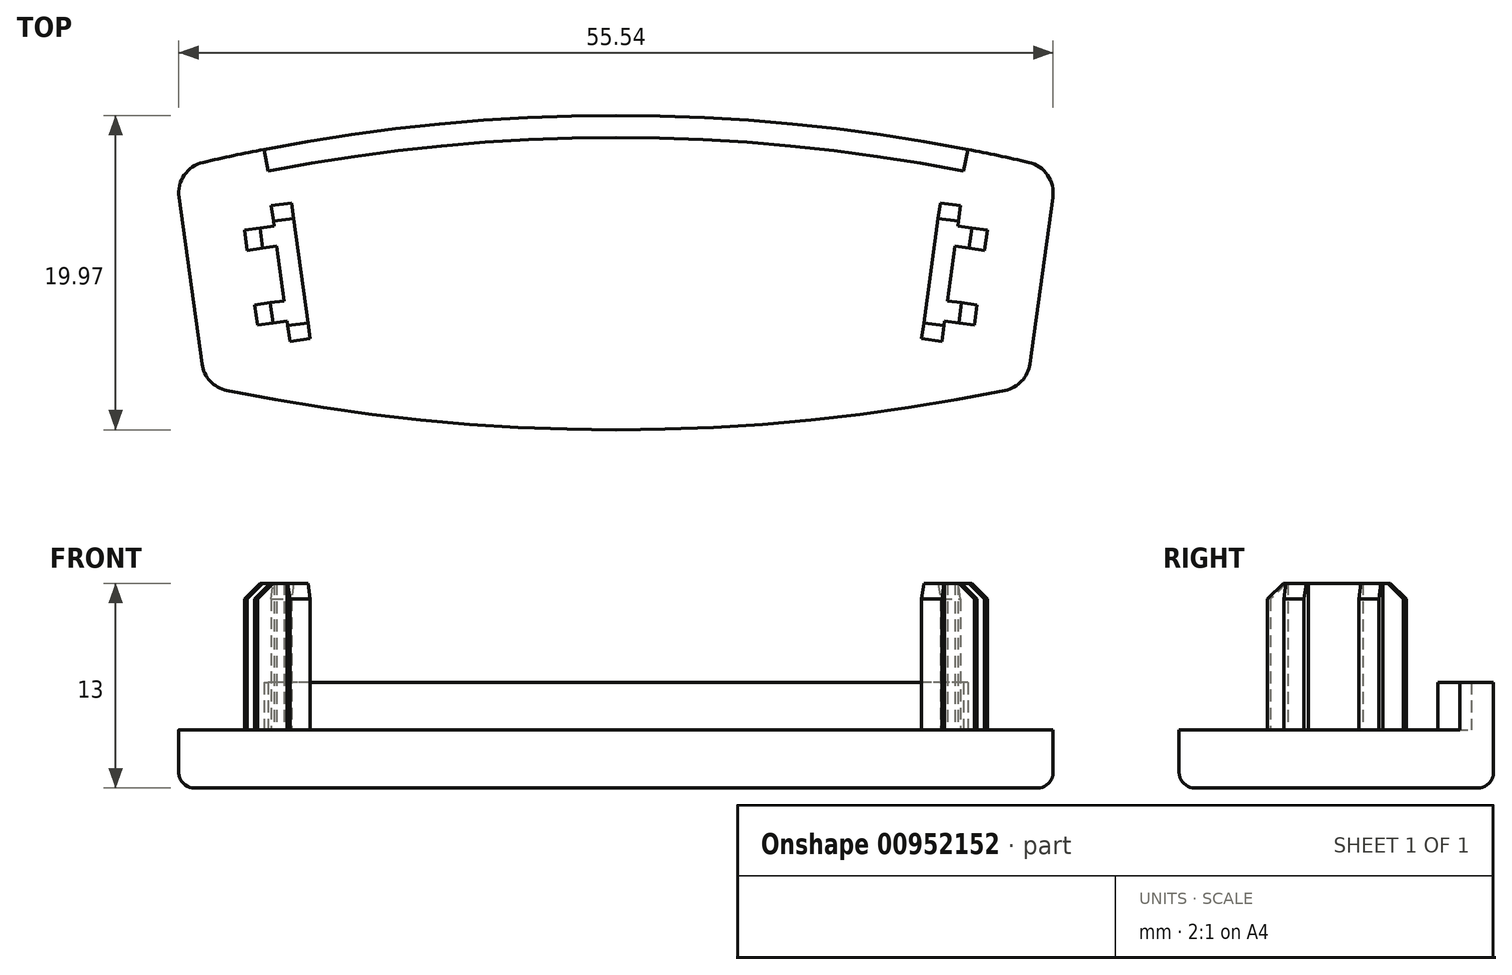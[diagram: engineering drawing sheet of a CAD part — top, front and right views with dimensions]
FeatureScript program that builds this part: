
annotation { "Feature Type Name" : "Feature", "Feature Type Description" : "" }
export const myFeature = defineFeature(function(context is Context, id is Id, definition is map)
    precondition{}
    {
        {
            var Q0;
            Q0=qCreatedBy(makeId("Top.planeOp"),FACE);
            var sketch = newSketch(context, id + "F0", { "sketchPlane" : qUnion([Q0])});
            skLineSegment(sketch, "E0", {"start": v(0, 0) * mm, "end": v(0, -117) * mm, "construction": true});
            skArc(sketch, "E1", {"start": v(28, -3.4) * mm, "mid": v(14.1, -0.85) * mm, "end": v(0, 0) * mm});
            skLineSegment(sketch, "E2", {"start": v(28, -3.4) * mm, "end": v(26.1, -17.17) * mm});
            skArc(sketch, "E3", {"start": v(0, -19.97) * mm, "mid": v(13.12, -19.27) * mm, "end": v(26.1, -17.17) * mm});
            skArc(sketch, "E4.MirrorCS", {"start": v(-28, -3.4) * mm, "mid": v(-14.1, -0.85) * mm, "end": v(0, 0) * mm});
            skLineSegment(sketch, "E5.MirrorCS", {"start": v(-28, -3.4) * mm, "end": v(-26.1, -17.17) * mm});
            skArc(sketch, "E6.MirrorCS", {"start": v(0, -19.97) * mm, "mid": v(-13.12, -19.27) * mm, "end": v(-26.1, -17.17) * mm});
            skSolve(sketch);
        }
        {
            var Q0;
            Q0 = qSketchRegion(id + "F0", true);
            extrude(context, id + "F1", {"entities" : qUnion([Q0]), "oppositeDirection" : true, "depth" : 3.7 * mm, "offsetDistance" : 25 * mm});
        }
        {
            var Q0;
            Q0=makeQuery(id+"F1.opExtrude","CAP_FACE",FACE,{"disambiguationData":[OSD([sQuery(id+"F0.wireOp",EDGE,"E1"),sQuery(id+"F0.wireOp",EDGE,"E2"),sQuery(id+"F0.wireOp",EDGE,"E3"),sQuery(id+"F0.wireOp",EDGE,"E4.MirrorCS"),sQuery(id+"F0.wireOp",EDGE,"E5.MirrorCS"),sQuery(id+"F0.wireOp",EDGE,"E6.MirrorCS")])],"isStart":true});
            var sketch = newSketch(context, id + "F2", { "sketchPlane" : qUnion([Q0])});
            skArc(sketch, "E7", {"start": v(22.35, -2.15) * mm, "mid": v(0, 0) * mm, "end": v(-22.35, -2.15) * mm});
            skPoint(sketch, "E8.end.orphan", {"position": v(-28, -3.4) * mm});
            skPoint(sketch, "E9.0.start.orphan", {"position": v(28, -3.4) * mm});
            skLineSegment(sketch, "E10", {"start": v(0, 0) * mm, "end": v(0, -19.97) * mm, "construction": true});
            skArc(sketch, "E11.0", {"start": v(22.08, -3.53) * mm, "mid": v(0, -1.4) * mm, "end": v(-22.08, -3.53) * mm});
            skLineSegment(sketch, "E12", {"start": v(-22.35, -2.15) * mm, "end": v(-22.08, -3.53) * mm});
            skLineSegment(sketch, "E13", {"start": v(22.35, -2.15) * mm, "end": v(22.08, -3.53) * mm});
            skPoint(sketch, "E14", {"position": v(0, -7.1) * mm});
            skLineSegment(sketch, "E15", {"start": v(0, -7.1) * mm, "end": v(21.3, -10.04) * mm, "construction": true});
            skLineSegment(sketch, "E16", {"start": v(21.9, -5.73) * mm, "end": v(20.7, -14.35) * mm});
            skLineSegment(sketch, "E17.0", {"start": v(20.6, -5.55) * mm, "end": v(19.42, -14.17) * mm});
            skLineSegment(sketch, "E18", {"start": v(21.9, -5.73) * mm, "end": v(20.6, -5.55) * mm});
            skLineSegment(sketch, "E19", {"start": v(20.7, -14.35) * mm, "end": v(19.42, -14.17) * mm});
            skLineSegment(sketch, "E20", {"start": v(21.72, -7.02) * mm, "end": v(23.6, -7.28) * mm});
            skLineSegment(sketch, "E21", {"start": v(23.6, -7.28) * mm, "end": v(23.42, -8.56) * mm});
            skLineSegment(sketch, "E22", {"start": v(23.42, -8.56) * mm, "end": v(21.54, -8.3) * mm});
            skLineSegment(sketch, "E23.MirrorCS", {"start": v(20.88, -13.06) * mm, "end": v(22.76, -13.32) * mm});
            skLineSegment(sketch, "E24.MirrorCS", {"start": v(22.76, -13.32) * mm, "end": v(22.94, -12.03) * mm});
            skLineSegment(sketch, "E25.MirrorCS", {"start": v(22.94, -12.03) * mm, "end": v(21.06, -11.77) * mm});
            skLineSegment(sketch, "E26.MirrorCS", {"start": v(-20.6, -5.55) * mm, "end": v(-19.42, -14.17) * mm});
            skLineSegment(sketch, "E27.MirrorCS", {"start": v(-21.9, -5.73) * mm, "end": v(-20.6, -5.55) * mm});
            skLineSegment(sketch, "E28.MirrorCS", {"start": v(-21.9, -5.73) * mm, "end": v(-20.7, -14.35) * mm});
            skLineSegment(sketch, "E29.MirrorCS", {"start": v(-21.72, -7.02) * mm, "end": v(-23.6, -7.28) * mm});
            skLineSegment(sketch, "E30.MirrorCS", {"start": v(-23.6, -7.28) * mm, "end": v(-23.42, -8.56) * mm});
            skLineSegment(sketch, "E31.MirrorCS", {"start": v(-23.42, -8.56) * mm, "end": v(-21.54, -8.3) * mm});
            skLineSegment(sketch, "E32.MirrorCS", {"start": v(-22.94, -12.03) * mm, "end": v(-21.06, -11.77) * mm});
            skLineSegment(sketch, "E33.MirrorCS", {"start": v(-22.76, -13.32) * mm, "end": v(-22.94, -12.03) * mm});
            skLineSegment(sketch, "E34.MirrorCS", {"start": v(-20.88, -13.06) * mm, "end": v(-22.76, -13.32) * mm});
            skLineSegment(sketch, "E35.MirrorCS", {"start": v(-20.7, -14.35) * mm, "end": v(-19.42, -14.17) * mm});
            skSolve(sketch);
        }
        {
            var Q0;
            Q0=makeQuery(id+"F2.imprint","IMPRINT",FACE,{"disambiguationData":[TD([[makeQuery(id+"F2.imprint","IMPRINT",EDGE,{"derivedFrom":sQuery(id+"F2.wireOp",EDGE,"E7")}),1.0]])]});
            var Q1;
            Q1=sQuery(id+"F2.wireOp",EDGE,"E7");
            var Q2;
            Q2=sQuery(id+"F2.wireOp",EDGE,"E12");
            var Q3;
            Q3=sQuery(id+"F2.wireOp",EDGE,"E11.0");
            var Q4;
            Q4=sQuery(id+"F2.wireOp",EDGE,"E13");
            extrude(context, id + "F3", {"entities" : qUnion([Q0]), "operationType" : NewBodyOperationType.ADD, "surfaceEntities" : qUnion([Q1, Q2, Q3, Q4]), "depth" : 3 * mm, "offsetDistance" : 25 * mm});
        }
        {
            var Q0;
            Q0=makeQuery(id+"F2.imprint","IMPRINT",FACE,{"disambiguationData":[TD([[makeQuery(id+"F2.imprint","IMPRINT",EDGE,{"derivedFrom":sQuery(id+"F2.wireOp",EDGE,"E17.0")}),1.0]])]});
            var Q1;
            {var subQ0=sQuery(id+"F2.wireOp",EDGE,"E20");Q1=makeQuery(id+"F2.imprint","IMPRINT",FACE,{"disambiguationData":[TD([[makeQuery(id+"F2.imprint","IMPRINT",EDGE,{"derivedFrom":subQ0}),-1.0]])]});}
            var Q2;
            {var subQ0=sQuery(id+"F2.wireOp",EDGE,"E23.MirrorCS");Q2=makeQuery(id+"F2.imprint","IMPRINT",FACE,{"disambiguationData":[TD([[makeQuery(id+"F2.imprint","IMPRINT",EDGE,{"derivedFrom":subQ0}),1.0]])]});}
            var Q3;
            Q3=makeQuery(id+"F2.imprint","IMPRINT",FACE,{"disambiguationData":[TD([[makeQuery(id+"F2.imprint","IMPRINT",EDGE,{"derivedFrom":sQuery(id+"F2.wireOp",EDGE,"E26.MirrorCS")}),-1.0]])]});
            var Q4;
            {var subQ0=sQuery(id+"F2.wireOp",EDGE,"E29.MirrorCS");Q4=makeQuery(id+"F2.imprint","IMPRINT",FACE,{"disambiguationData":[TD([[makeQuery(id+"F2.imprint","IMPRINT",EDGE,{"derivedFrom":subQ0}),1.0]])]});}
            var Q5;
            {var subQ0=sQuery(id+"F2.wireOp",EDGE,"E32.MirrorCS");Q5=makeQuery(id+"F2.imprint","IMPRINT",FACE,{"disambiguationData":[TD([[makeQuery(id+"F2.imprint","IMPRINT",EDGE,{"derivedFrom":subQ0}),-1.0]])]});}
            extrude(context, id + "F4", {"entities" : qUnion([Q0, Q1, Q2, Q3, Q4, Q5]), "operationType" : NewBodyOperationType.ADD, "depth" : 9.3 * mm, "offsetDistance" : 25 * mm});
        }
        {
            var Q0;
            Q0=makeQuery(id+"F1.opExtrude","SWEPT_EDGE",EDGE,{"disambiguationData":[OSD([sQuery(id+"F0.wireOp",EDGE,"E1"),sQuery(id+"F0.wireOp",EDGE,"E2")])]});
            var Q1;
            Q1=makeQuery(id+"F1.opExtrude","SWEPT_EDGE",EDGE,{"disambiguationData":[OSD([sQuery(id+"F0.wireOp",EDGE,"E2"),sQuery(id+"F0.wireOp",EDGE,"E3")])]});
            var Q2;
            Q2=makeQuery(id+"F1.opExtrude","SWEPT_EDGE",EDGE,{"disambiguationData":[OSD([sQuery(id+"F0.wireOp",EDGE,"E4.MirrorCS"),sQuery(id+"F0.wireOp",EDGE,"E5.MirrorCS")])]});
            var Q3;
            Q3=makeQuery(id+"F1.opExtrude","SWEPT_EDGE",EDGE,{"disambiguationData":[OSD([sQuery(id+"F0.wireOp",EDGE,"E5.MirrorCS"),sQuery(id+"F0.wireOp",EDGE,"E6.MirrorCS")])]});
            fillet(context, id + "F5", {"entities" : qUnion([Q0, Q1, Q2, Q3]), "radius" : 2 * mm, "tangentPropagation" : true, "allowEdgeOverflow" : false});
        }
        {
            var Q0;
            Q0=makeQuery(id+"F4.opExtrude","CAP_EDGE",EDGE,{"disambiguationData":[OSD([sQuery(id+"F2.wireOp",EDGE,"E27.MirrorCS")])],"isStart":false});
            var Q1;
            Q1=makeQuery(id+"F4.opExtrude","CAP_EDGE",EDGE,{"disambiguationData":[OSD([sQuery(id+"F2.wireOp",EDGE,"E30.MirrorCS")])],"isStart":false});
            var Q2;
            Q2=makeQuery(id+"F4.opExtrude","CAP_EDGE",EDGE,{"disambiguationData":[OSD([sQuery(id+"F2.wireOp",EDGE,"E33.MirrorCS")])],"isStart":false});
            var Q3;
            Q3=makeQuery(id+"F4.opExtrude","CAP_EDGE",EDGE,{"disambiguationData":[OSD([sQuery(id+"F2.wireOp",EDGE,"E35.MirrorCS")])],"isStart":false});
            var Q4;
            Q4=makeQuery(id+"F4.opExtrude","CAP_EDGE",EDGE,{"disambiguationData":[OSD([sQuery(id+"F2.wireOp",EDGE,"E18")])],"isStart":false});
            var Q5;
            Q5=makeQuery(id+"F4.opExtrude","CAP_EDGE",EDGE,{"disambiguationData":[OSD([sQuery(id+"F2.wireOp",EDGE,"E21")])],"isStart":false});
            var Q6;
            Q6=makeQuery(id+"F4.opExtrude","CAP_EDGE",EDGE,{"disambiguationData":[OSD([sQuery(id+"F2.wireOp",EDGE,"E24.MirrorCS")])],"isStart":false});
            var Q7;
            Q7=makeQuery(id+"F4.opExtrude","CAP_EDGE",EDGE,{"disambiguationData":[OSD([sQuery(id+"F2.wireOp",EDGE,"E19")])],"isStart":false});
            chamfer(context, id + "F6", {"entities" : qUnion([Q0, Q1, Q2, Q3, Q4, Q5, Q6, Q7]), "width" : 1 * mm, "tangentPropagation" : true});
        }
        {
            var Q0;
            Q0=makeQuery(id+"F1.opExtrude","CAP_FACE",FACE,{"disambiguationData":[OSD([sQuery(id+"F0.wireOp",EDGE,"E1"),sQuery(id+"F0.wireOp",EDGE,"E2"),sQuery(id+"F0.wireOp",EDGE,"E3"),sQuery(id+"F0.wireOp",EDGE,"E4.MirrorCS"),sQuery(id+"F0.wireOp",EDGE,"E5.MirrorCS"),sQuery(id+"F0.wireOp",EDGE,"E6.MirrorCS")])],"isStart":false});
            fillet(context, id + "F7", {"entities" : qUnion([Q0]), "radius" : 1 * mm, "tangentPropagation" : true, "allowEdgeOverflow" : false});
        }
    });
